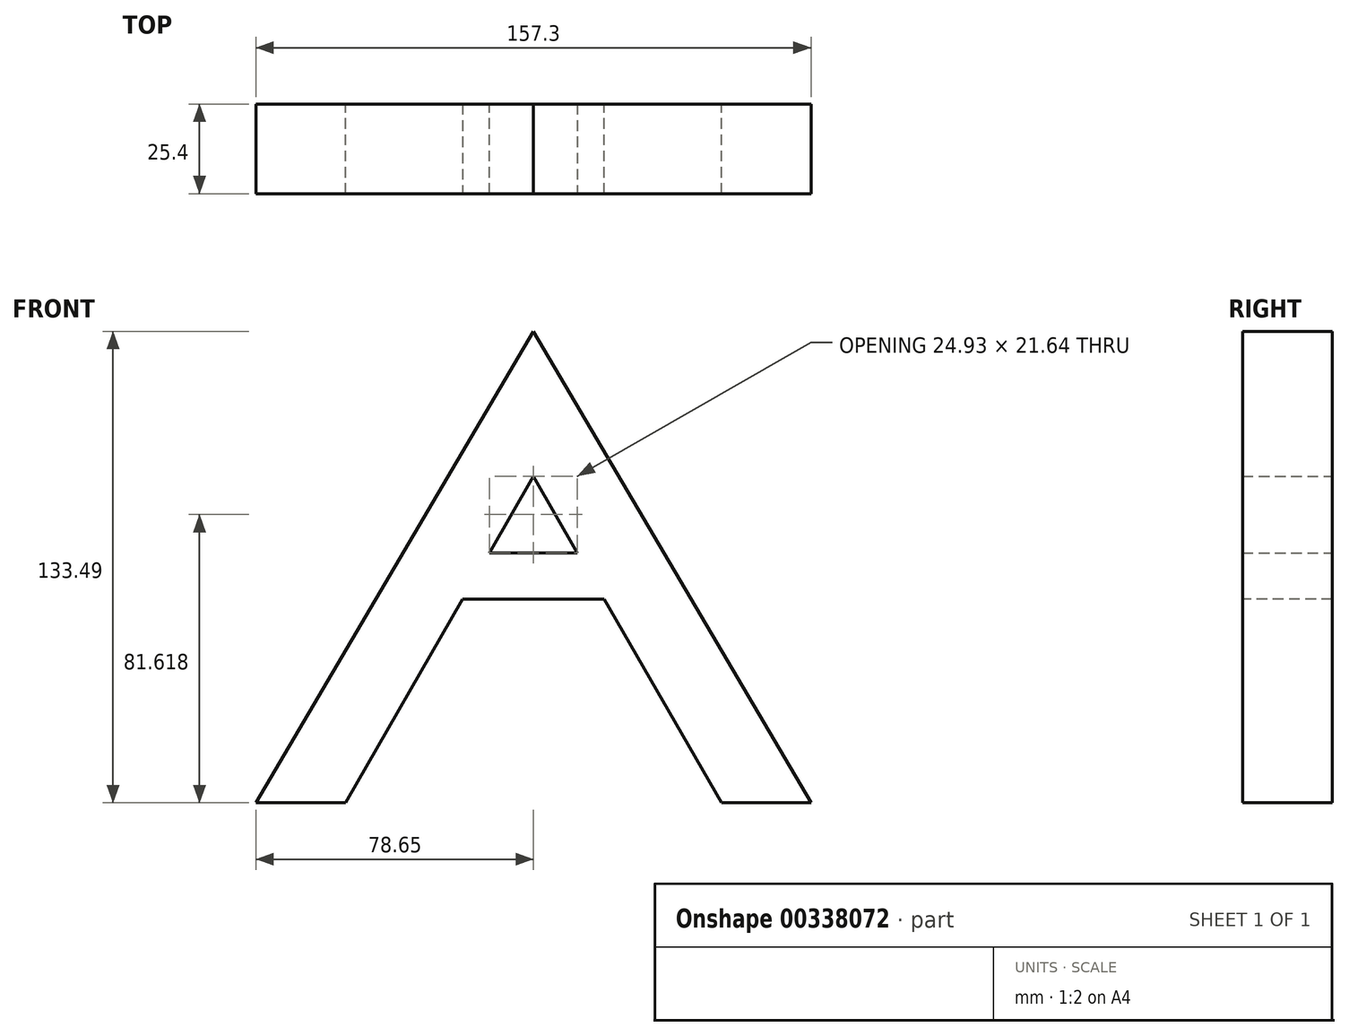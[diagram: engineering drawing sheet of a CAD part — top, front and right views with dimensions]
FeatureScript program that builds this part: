
annotation { "Feature Type Name" : "Feature", "Feature Type Description" : "" }
export const myFeature = defineFeature(function(context is Context, id is Id, definition is map)
    precondition{}
    {
        {
            var Q0;
            Q0=qCreatedBy(makeId("Front.planeOp"),FACE);
            var sketch = newSketch(context, id + "F0", { "sketchPlane" : qUnion([Q0])});
            skLineSegment(sketch, "E0", {"start": v(0, 75.9) * mm, "end": v(-78.65, -57.6) * mm});
            skLineSegment(sketch, "E1", {"start": v(-78.65, -57.6) * mm, "end": v(-53.25, -57.6) * mm});
            skLineSegment(sketch, "E2", {"start": v(-53.25, -57.6) * mm, "end": v(0, 34.84) * mm});
            skLineSegment(sketch, "E3", {"start": v(0, 34.84) * mm, "end": v(53.25, -57.6) * mm});
            skLineSegment(sketch, "E4", {"start": v(53.25, -57.6) * mm, "end": v(78.65, -57.6) * mm});
            skLineSegment(sketch, "E5", {"start": v(78.65, -57.6) * mm, "end": v(0, 75.9) * mm});
            skSolve(sketch);
        }
        {
            var Q0;
            Q0=qCreatedBy(makeId("Front.planeOp"),FACE);
            var sketch = newSketch(context, id + "F1", { "sketchPlane" : qUnion([Q0])});
            skLineSegment(sketch, "E6", {"start": v(-29.13, 13.2) * mm, "end": v(21.67, 13.2) * mm});
            skLineSegment(sketch, "E7", {"start": v(21.67, 13.2) * mm, "end": v(29.29, 0) * mm});
            skLineSegment(sketch, "E8", {"start": v(29.29, 0) * mm, "end": v(-36.75, 0) * mm});
            skLineSegment(sketch, "E9", {"start": v(-36.75, 0) * mm, "end": v(-29.13, 13.2) * mm});
            skSolve(sketch);
        }
        {
            var Q0;
            Q0=makeQuery(id+"F0.imprint","IMPRINT",FACE,{"disambiguationData":[TD([[makeQuery(id+"F0.imprint","IMPRINT",EDGE,{"derivedFrom":sQuery(id+"F0.wireOp",EDGE,"E0")}),1.0]])]});
            extrude(context, id + "F2", {"entities" : qUnion([Q0]), "depth" : 25.4 * mm});
        }
        {
            var Q0;
            Q0=makeQuery(id+"F1.imprint","IMPRINT",FACE,{"disambiguationData":[TD([[makeQuery(id+"F1.imprint","IMPRINT",EDGE,{"derivedFrom":sQuery(id+"F1.wireOp",EDGE,"E6")}),-1.0]])]});
            extrude(context, id + "F3", {"entities" : qUnion([Q0]), "operationType" : NewBodyOperationType.ADD, "depth" : 25.4 * mm});
        }
    });
